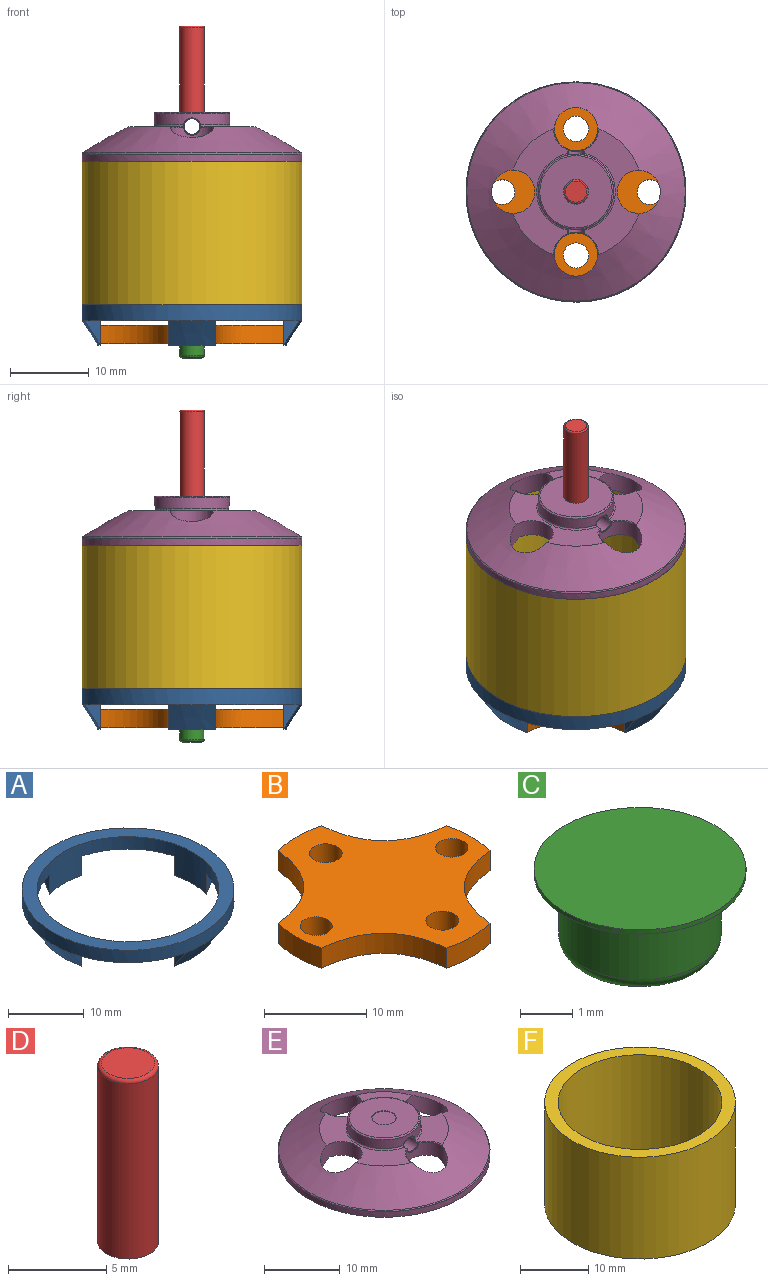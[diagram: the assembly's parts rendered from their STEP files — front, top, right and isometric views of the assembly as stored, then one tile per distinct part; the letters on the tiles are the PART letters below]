
ASSEMBLY  parts=6 mates=5
PART A: 19 faces, bbox 28x28x5.1 mm
  f0: plane 10.67x10.67mm, normal (0,0,-1), area 28.4mm2, adj f7,f9,f11,f12
  f1: plane 10.67x10.67mm, normal (0,0,-1), area 28.4mm2, adj f7,f9,f17,f18
  f2: plane 10.67x10.67mm, normal (0,0,-1), area 28.4mm2, adj f7,f9,f15,f16
  f3: plane 28x28mm, normal (0,0,1), area 161.6mm2, adj f7,f9
  f4: cone r=14mm half-angle=32.4deg, axis (0,0,1), area 22.4mm2, adj f7,f9,f12,f17
  f5: cone r=14mm half-angle=32.4deg, axis (0,0,1), area 22.4mm2, adj f7,f9,f15,f18
  f6: cone r=14mm half-angle=32.4deg, axis (0,0,1), area 22.4mm2, adj f7,f9,f13,f16
  f7: cylinder r=14mm len=28mm, axis (0,0,1), area 175.9mm2, adj f0,f1,f2,f3,f4,f5,f6,f8
  f8: cone r=14mm half-angle=32.4deg, axis (0,0,1), area 22.4mm2, adj f7,f9,f11,f14
  f9: cylinder r=12.02mm len=24.05mm, axis (0,0,1), area 226.6mm2, adj f0,f1,f2,f3,f4,f5,f6,f8
  f10: plane 10.67x10.67mm, normal (0,0,-1), area 28.4mm2, adj f7,f9,f13,f14
  f11: plane 3.15x2.07mm, normal (1,0,0), area 3.2mm2, adj f0,f8,f9
  f12: plane 3.15x2.07mm, normal (0,1,0), area 3.2mm2, adj f0,f4,f9
  f13: plane 3.15x2.07mm, normal (0,1,0), area 3.2mm2, adj f6,f9,f10
  f14: plane 3.15x2.07mm, normal (-1,0,0), area 3.2mm2, adj f8,f9,f10
  f15: plane 3.15x2.07mm, normal (-1,0,0), area 3.2mm2, adj f2,f5,f9
  f16: plane 3.15x2.07mm, normal (0,-1,0), area 3.2mm2, adj f2,f6,f9
  f17: plane 3.15x2.07mm, normal (0,-1,0), area 3.2mm2, adj f1,f4,f9
  f18: plane 3.15x2.07mm, normal (1,0,0), area 3.2mm2, adj f1,f5,f9
PART B: 20 faces, bbox 24x24x2.4 mm
  f0: plane 7.79x7.79mm, normal (0,0,-1), area 47.7mm2, adj f11
  f1: plane 24.05x24.05mm, normal (0,0,1), area 284.9mm2, adj f2,f3,f4,f5,f6,f7,f8,f9
  f2: cylinder r=12.02mm len=6mm, axis (0,0,-1), area 14.6mm2, adj f1,f3,f9,f10
  f3: extruded ~8.64x8.64mm, area 32.4mm2, adj f1,f2,f4,f10
  f4: cylinder r=12.02mm len=6mm, axis (0,0,-1), area 14.6mm2, adj f1,f3,f5,f10
  f5: extruded ~8.64x8.64mm, area 32.4mm2, adj f1,f4,f6,f10
  f6: cylinder r=12.02mm len=6mm, axis (0,0,-1), area 14.6mm2, adj f1,f5,f7,f10
  f7: extruded ~8.64x8.64mm, area 32.4mm2, adj f1,f6,f8,f10
  f8: cylinder r=12.02mm len=6mm, axis (0,0,-1), area 14.6mm2, adj f1,f7,f9,f10
  f9: extruded ~8.64x8.64mm, area 32.4mm2, adj f1,f2,f8,f10
  f10: plane 24.05x24.05mm, normal (0,0,-1), area 225.7mm2, adj f2,f3,f4,f5,f6,f7,f8,f9
  f11: cone r=3.49mm half-angle=71deg, axis (0,0,-1), area 7.8mm2, adj f0,f10
  f12: cylinder r=1.57mm len=3.15mm, axis (0,0,-1), area 22.8mm2, adj f1,f14
  f13: cylinder r=1.57mm len=3.15mm, axis (0,0,-1), area 22.8mm2, adj f1,f15
  f14: torus R=1.68mm, axis (0,0,1), area 1.6mm2, adj f10,f12
  f15: torus R=1.68mm, axis (0,0,1), area 1.6mm2, adj f10,f13
  f16: cylinder r=1.6mm len=3.2mm, axis (0,0,-1), area 23.1mm2, adj f1,f19
  f17: cylinder r=1.6mm len=3.2mm, axis (0,0,-1), area 23.1mm2, adj f1,f18
  f18: torus R=1.7mm, axis (0,0,1), area 1.6mm2, adj f10,f17
  f19: torus R=1.7mm, axis (0,0,1), area 1.6mm2, adj f10,f16
PART C: 6 faces, bbox 4x4x1.8 mm
  f0: plane 4.04x4.04mm, normal (0,0,-1), area 5.3mm2, adj f1,f4
  f1: cylinder r=2.02mm len=4.04mm, axis (0,0,1), area 1.3mm2, adj f0,f5
  f2: plane 2.5x2.5mm, normal (0,0,-1), area 4.9mm2, adj f3
  f3: torus R=1.25mm, axis (0,0,-1), area 4.3mm2, adj f2,f4
  f4: cylinder r=1.55mm len=3.1mm, axis (0,0,1), area 13.6mm2, adj f0,f3
  f5: plane 4.04x4.04mm, normal (0,0,1), area 12.8mm2, adj f1
PART D: 4 faces, bbox 3.4x3.4x11.1 mm
  f0: plane 2.7x2.7mm, normal (0,0,1), area 5.7mm2, adj f3
  f1: cylinder r=1.55mm len=10.9mm, axis (0,0,-1), area 106.2mm2, adj f2,f3
  f2: plane 3.1x3.1mm, normal (0,0,-1), area 7.5mm2, adj f1
  f3: torus R=1.35mm, axis (0,0,1), area 2.9mm2, adj f0,f1
PART E: 40 faces, bbox 30.3x30.3x6.2 mm
  f0: plane 9.2x9.2mm, normal (0,0,1), area 58.5mm2, adj f10,f38
  f1: plane 16.02x6.95mm, normal (0,0,1), area 45mm2, adj f2,f6,f14,f22,f23,f28,f37
  f2: torus R=5mm, axis (0,0,1), area 4.1mm2, adj f1,f8,f21,f29
  f3: plane 16.02x6.95mm, normal (0,0,1), area 45mm2, adj f6,f9,f12,f18,f27,f32,f33
  f4: cylinder r=14mm len=28mm, axis (0,0,-1), area 78.2mm2, adj f5,f7
  f5: plane 28x28mm, normal (0,0,-1), area 190.4mm2, adj f4,f15
  f6: cone r=8.5mm half-angle=58.3deg, axis (0,0,-1), area 400.9mm2, adj f1,f3,f7,f11,f12,f13,f14,f23
  f7: torus R=13.8mm, axis (0,0,-1), area 17.9mm2, adj f4,f6
  f8: cylinder r=4.8mm len=9.6mm, axis (0,0,-1), area 39.2mm2, adj f2,f9,f10,f20,f30
  f9: torus R=5mm, axis (0,0,1), area 4.1mm2, adj f3,f8,f19,f31
  f10: torus R=4.6mm, axis (0,0,1), area 9.3mm2, adj f0,f8
  f11: cylinder r=2.75mm len=5.5mm, axis (0,0,1), area 38.4mm2, adj f6,f15,f16,f23,f25,f27
  f12: cylinder r=2.75mm len=5.5mm, axis (0,0,1), area 41mm2, adj f3,f6,f15,f16
  f13: cylinder r=2.75mm len=5.5mm, axis (0,0,1), area 38.4mm2, adj f6,f15,f16,f33,f35,f37
  f14: cylinder r=2.75mm len=5.5mm, axis (0,0,1), area 41mm2, adj f1,f6,f15,f16
  f15: cone r=7.87mm half-angle=59.7deg, axis (0,0,-1), area 205.5mm2, adj f5,f11,f12,f13,f14,f16
  f16: plane 14.78x14.78mm, normal (0,0,-1), area 152.9mm2, adj f11,f12,f13,f14,f15
  f17: cylinder r=1mm len=10.7mm, axis (0,-1,0), area 61.8mm2, adj f18,f19,f20,f21,f22,f25,f28,f29
  f18: cylinder r=0.1mm len=0.47mm, axis (0,-1,0), area 0.1mm2, adj f3,f17,f19,f26
  f19: bspline ~0.34x0.32mm, area 0.1mm2, adj f9,f17,f18,f20
  f20: bspline ~2.25x1.14mm, area 0.5mm2, adj f8,f17,f19,f21
  f21: bspline ~0.37x0.3mm, area 0.1mm2, adj f2,f17,f20,f22
  f22: cylinder r=0.1mm len=0.47mm, axis (0,-1,0), area 0.1mm2, adj f1,f17,f21,f24
  f23: torus R=2.85mm, axis (0,0,1), area 0.5mm2, adj f1,f6,f11,f24
  f24: sphere r=0.1mm, area 0mm2, adj f22,f23,f25
  f25: bspline ~2.13x1.23mm, area 0.4mm2, adj f11,f17,f24,f26
  f26: sphere r=0.1mm, area 0mm2, adj f18,f25,f27
  f27: torus R=2.85mm, axis (0,0,1), area 0.5mm2, adj f3,f6,f11,f26
  f28: cylinder r=0.1mm len=0.47mm, axis (0,-1,0), area 0.1mm2, adj f1,f17,f29,f36
  f29: bspline ~0.34x0.32mm, area 0.1mm2, adj f2,f17,f28,f30
  f30: bspline ~2.25x1.14mm, area 0.5mm2, adj f8,f17,f29,f31
  f31: bspline ~0.37x0.3mm, area 0.1mm2, adj f9,f17,f30,f32
  f32: cylinder r=0.1mm len=0.47mm, axis (0,-1,0), area 0.1mm2, adj f3,f17,f31,f34
  f33: torus R=2.85mm, axis (0,0,1), area 0.5mm2, adj f3,f6,f13,f34
  f34: sphere r=0.1mm, area 0mm2, adj f32,f33,f35
  f35: bspline ~2.13x1.23mm, area 0.4mm2, adj f13,f17,f34,f36
  f36: sphere r=0.1mm, area 0mm2, adj f28,f35,f37
  f37: torus R=2.85mm, axis (0,0,1), area 0.5mm2, adj f1,f6,f13,f36
  f38: cylinder r=1.59mm len=3.19mm, axis (0,0,1), area 1mm2, adj f0,f39
  f39: plane 3.19x3.19mm, normal (0,0,1), area 8mm2, adj f38
PART F: 4 faces, bbox 28x28x18.3 mm
  f0: cylinder r=14mm len=28mm, axis (0,0,-1), area 1609.8mm2, adj f1,f2
  f1: plane 28x28mm, normal (0,0,1), area 161.6mm2, adj f0,f3
  f2: plane 28x28mm, normal (0,0,-1), area 161.6mm2, adj f0,f3
  f3: cylinder r=12.02mm len=24.05mm, axis (0,0,-1), area 1382.4mm2, adj f1,f2
PLACE A t=(-2.39,3.65,-6.15)mm
PLACE B t=(-2.39,3.65,-5.99)mm
PLACE C t=(-2.39,3.65,-5.99)mm
PLACE D t=(-2.39,3.65,-6.95)mm
PLACE E t=(-2.39,3.65,-6.85)mm
PLACE F t=(-2.39,3.65,-6.65)mm fixed
MATE fastened B.f2 <-> A.f4  axis (0,0,1) through (-2.39,3.65,-9.21)mm
MATE fastened A.f4 <-> F.f0  axis (0,0,1) through (-2.39,3.65,-6.65)mm
MATE fastened C.f1 <-> B.f2  axis (0,0,1) through (-2.39,3.65,-11.61)mm
MATE fastened E.f2 <-> F.f0  axis (0,0,-1) through (-2.39,3.65,11.65)mm
MATE fastened D.f1 <-> E.f2  axis (0,0,-1) through (-2.39,3.65,17.75)mm
